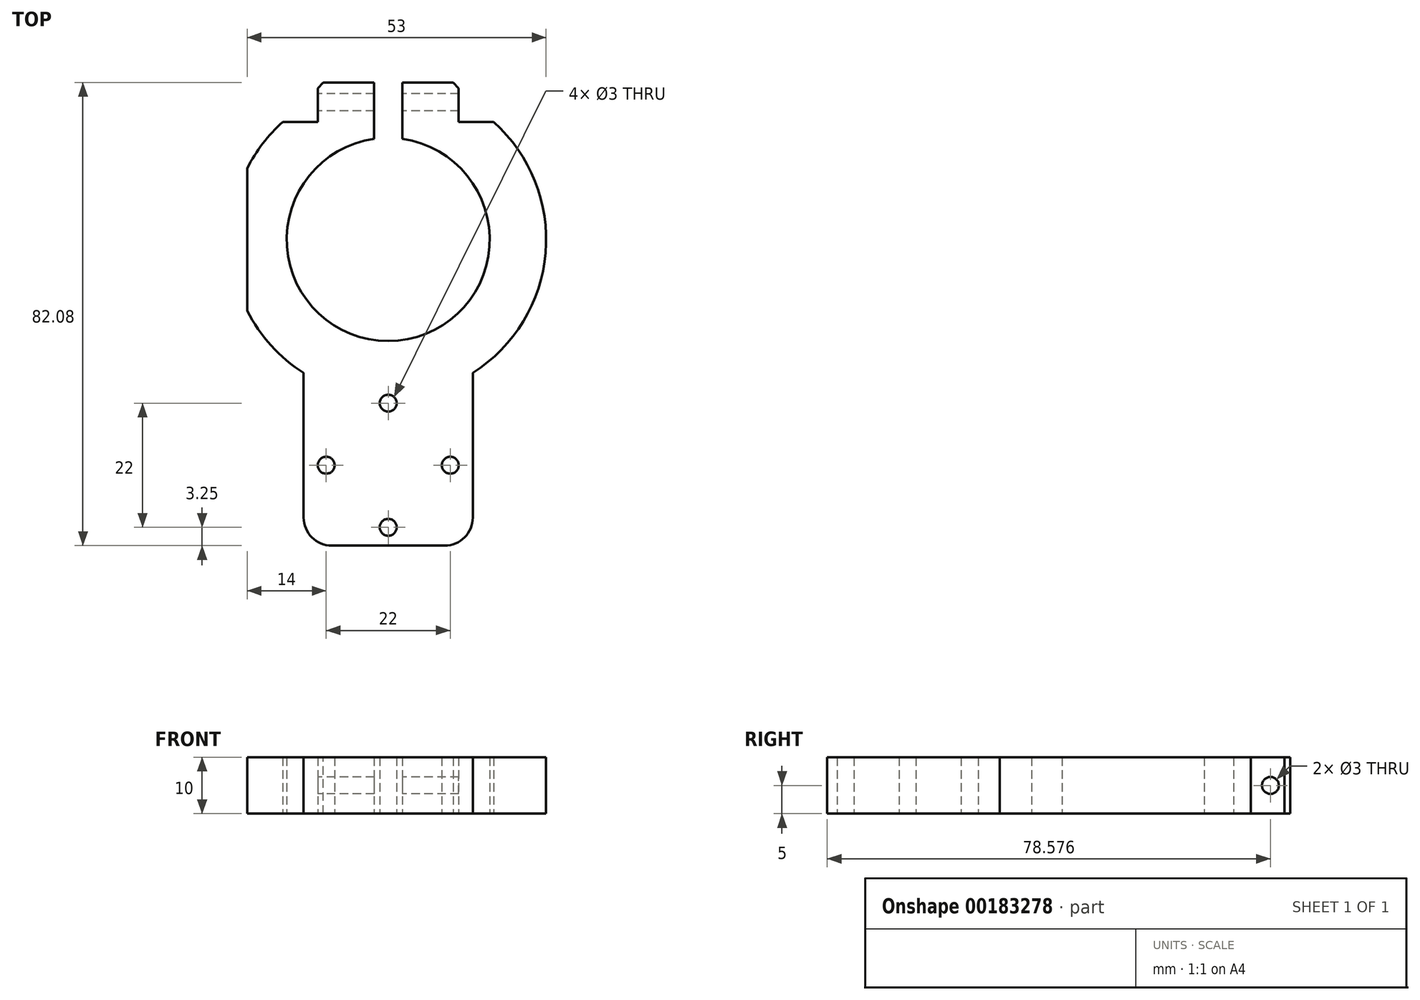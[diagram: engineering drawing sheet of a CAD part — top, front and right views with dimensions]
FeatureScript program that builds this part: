
annotation { "Feature Type Name" : "Feature", "Feature Type Description" : "" }
export const myFeature = defineFeature(function(context is Context, id is Id, definition is map)
    precondition{}
    {
        {
            var Q0;
            Q0=qCreatedBy(makeId("Top.planeOp"),FACE);
            var sketch = newSketch(context, id + "F0", { "sketchPlane" : qUnion([Q0])});
            skArc(sketch, "E0", {"start": v(0, -18) * mm, "mid": v(-17.96, -1.25) * mm, "end": v(-2.5, 17.83) * mm});
            skArc(sketch, "E1", {"start": v(-15, -23.64) * mm, "mid": v(-27.9, -2.33) * mm, "end": v(-18.72, 20.83) * mm});
            skLineSegment(sketch, "E2", {"start": v(-15, -23.64) * mm, "end": v(-15, -54.25) * mm});
            skLineSegment(sketch, "E3", {"start": v(-15, -54.25) * mm, "end": v(0, -54.25) * mm});
            skLineSegment(sketch, "E4", {"start": v(-18, 0) * mm, "end": v(-28, 0) * mm, "construction": true});
            skLineSegment(sketch, "E5", {"start": v(-2.5, 17.83) * mm, "end": v(-2.5, 27.83) * mm});
            skLineSegment(sketch, "E6", {"start": v(-12.5, 27.83) * mm, "end": v(-2.5, 27.83) * mm});
            skCircle(sketch, "E7", {"center": v(0, 0) * mm, "radius": 18 * mm, "construction": true});
            skLineSegment(sketch, "E8", {"start": v(-12.5, 27.83) * mm, "end": v(-12.5, 20.83) * mm});
            skLineSegment(sketch, "E9", {"start": v(-12.5, 20.83) * mm, "end": v(-18.72, 20.83) * mm});
            skArc(sketch, "E10.MirrorCS", {"start": v(0, -18) * mm, "mid": v(17.96, -1.25) * mm, "end": v(2.5, 17.83) * mm});
            skLineSegment(sketch, "E11.MirrorCS", {"start": v(15, -54.25) * mm, "end": v(0, -54.25) * mm});
            skArc(sketch, "E12.MirrorCS", {"start": v(15, -23.64) * mm, "mid": v(27.9, -2.33) * mm, "end": v(18.72, 20.83) * mm});
            skLineSegment(sketch, "E13.MirrorCS", {"start": v(12.5, 20.83) * mm, "end": v(18.72, 20.83) * mm});
            skLineSegment(sketch, "E14.MirrorCS", {"start": v(15, -23.64) * mm, "end": v(15, -54.25) * mm});
            skLineSegment(sketch, "E15.MirrorCS", {"start": v(12.5, 27.83) * mm, "end": v(12.5, 20.83) * mm});
            skLineSegment(sketch, "E16.MirrorCS", {"start": v(18, 0) * mm, "end": v(28, 0) * mm, "construction": true});
            skLineSegment(sketch, "E17.MirrorCS", {"start": v(12.5, 27.83) * mm, "end": v(2.5, 27.83) * mm});
            skLineSegment(sketch, "E18.MirrorCS", {"start": v(2.5, 17.83) * mm, "end": v(2.5, 27.83) * mm});
            skCircle(sketch, "E19", {"center": v(0, -40) * mm, "radius": 14.25 * mm, "construction": true});
            skCircle(sketch, "E20", {"center": v(0, -40) * mm, "radius": 11 * mm, "construction": true});
            skCircle(sketch, "E21", {"center": v(0, -51) * mm, "radius": 1.5 * mm});
            skCircle(sketch, "E22", {"center": v(-11, -40) * mm, "radius": 1.5 * mm});
            skCircle(sketch, "E23", {"center": v(0, -29) * mm, "radius": 1.5 * mm});
            skCircle(sketch, "E24", {"center": v(11, -40) * mm, "radius": 1.5 * mm});
            skLineSegment(sketch, "E25", {"start": v(-11, -40) * mm, "end": v(11, -40) * mm, "construction": true});
            skSolve(sketch);
        }
        {
            var Q0;
            Q0 = qSketchRegion(id + "F0", true);
            extrude(context, id + "F1", {"entities" : qUnion([Q0]), "endBound" : BoundingType.SYMMETRIC, "depth" : 10 * mm});
        }
        {
            var Q0;
            Q0=makeQuery(id+"F1.opExtrude","SWEPT_FACE",FACE,{"disambiguationData":[OSD([sQuery(id+"F0.wireOp",EDGE,"E8")])]});
            var sketch = newSketch(context, id + "F2", { "sketchPlane" : qUnion([Q0])});
            skCircle(sketch, "E26", {"center": v(-24.33, 0) * mm, "radius": 1.5 * mm});
            skSolve(sketch);
        }
        {
            var Q0;
            Q0 = qSketchRegion(id + "F2", true);
            extrude(context, id + "F3", {"entities" : qUnion([Q0]), "operationType" : NewBodyOperationType.REMOVE, "endBound" : BoundingType.THROUGH_ALL, "oppositeDirection" : true, "depth" : 25 * mm});
        }
        {
            var Q0;
            Q0=makeQuery(id+"F1.opExtrude","SWEPT_EDGE",EDGE,{"disambiguationData":[OSD([sQuery(id+"F0.wireOp",EDGE,"E15.MirrorCS"),sQuery(id+"F0.wireOp",EDGE,"E17.MirrorCS")])]});
            var Q1;
            Q1=makeQuery(id+"F1.opExtrude","SWEPT_EDGE",EDGE,{"disambiguationData":[OSD([sQuery(id+"F0.wireOp",EDGE,"E6"),sQuery(id+"F0.wireOp",EDGE,"E8")])]});
            chamfer(context, id + "F4", {"entities" : qUnion([Q0, Q1]), "width" : 1 * mm, "tangentPropagation" : true});
        }
        {
            var Q0;
            Q0=makeQuery(id+"F1.opExtrude","SWEPT_EDGE",EDGE,{"disambiguationData":[OSD([sQuery(id+"F0.wireOp",EDGE,"E2"),sQuery(id+"F0.wireOp",EDGE,"E3")])]});
            var Q1;
            Q1=makeQuery(id+"F1.opExtrude","SWEPT_EDGE",EDGE,{"disambiguationData":[OSD([sQuery(id+"F0.wireOp",EDGE,"E11.MirrorCS"),sQuery(id+"F0.wireOp",EDGE,"E14.MirrorCS")])]});
            fillet(context, id + "F5", {"entities" : qUnion([Q0, Q1]), "radius" : 5 * mm, "tangentPropagation" : true, "allowEdgeOverflow" : false});
        }
        {
            var Q0;
            Q0=qCreatedBy(makeId("Right.planeOp"),FACE);
            var Q1;
            Q1=sQuery(id+"F0.wireOp",VERTEX,"E4.end");
            cPlane(context, id + "F6", {"entities" : qUnion([Q0, Q1]), "cplaneType" : CPlaneType.PLANE_POINT, "offset" : 25 * mm, "width" : 150 * mm, "height" : 150 * mm});
        }
        {
            var Q0;
            Q0=qCreatedBy(id+"F6.planeOp",FACE);
            var sketch = newSketch(context, id + "F7", { "sketchPlane" : qUnion([Q0])});
            skLineSegment(sketch, "E27.bottom", {"start": v(20.83, 5) * mm, "end": v(-23.64, 5) * mm});
            skLineSegment(sketch, "E27.top", {"start": v(20.83, -5) * mm, "end": v(-23.64, -5) * mm});
            skLineSegment(sketch, "E27.left", {"start": v(20.83, 5) * mm, "end": v(20.83, -5) * mm});
            skLineSegment(sketch, "E27.right", {"start": v(-23.64, 5) * mm, "end": v(-23.64, -5) * mm});
            skSolve(sketch);
        }
        {
            var Q0;
            Q0=makeQuery(id+"F7.imprint","IMPRINT",FACE,{"disambiguationData":[TD([[makeQuery(id+"F7.imprint","IMPRINT",EDGE,{"derivedFrom":sQuery(id+"F7.wireOp",EDGE,"E27.bottom")}),1.0]])]});
            extrude(context, id + "F8", {"entities" : qUnion([Q0]), "operationType" : NewBodyOperationType.REMOVE, "depth" : 3 * mm});
        }
    });
